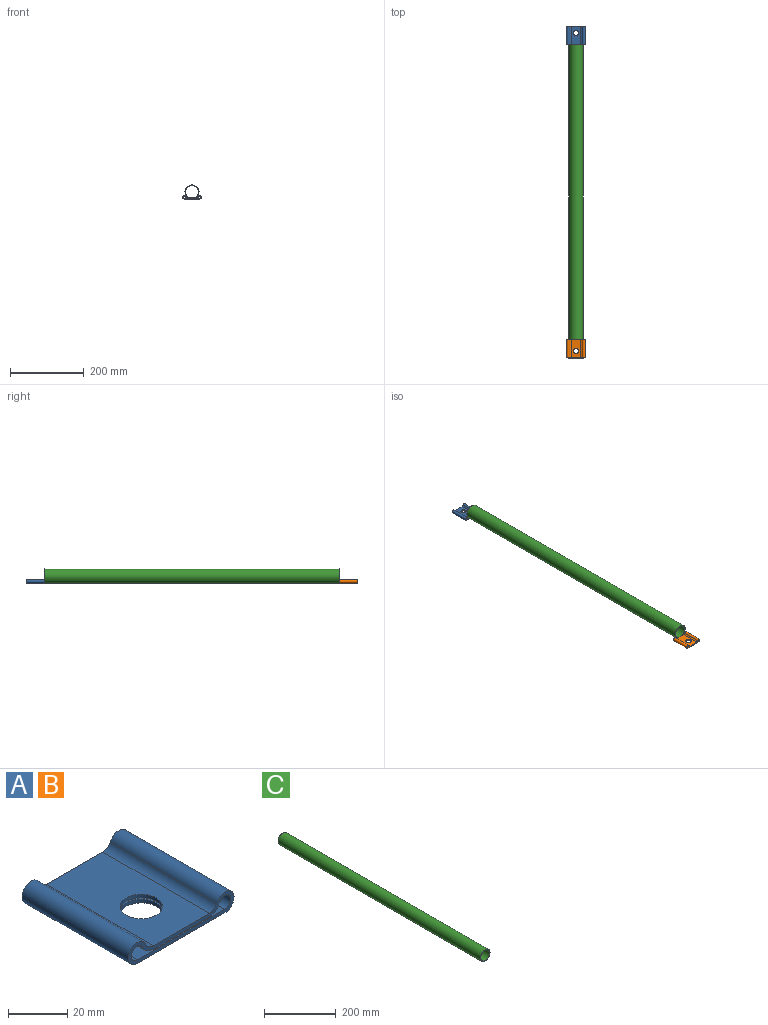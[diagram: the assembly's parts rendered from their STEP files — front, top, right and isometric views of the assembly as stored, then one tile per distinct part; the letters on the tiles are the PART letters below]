
ASSEMBLY  parts=3 mates=2
PART A: 16 faces, bbox 50.5x50.8x8.6 mm
  f0: cylinder r=3.81mm len=50.8mm, axis (0,1,0), area 230.1mm2, adj f1,f11,f12,f13
  f1: cylinder r=4.32mm len=50.8mm, axis (0,1,0), area 949.9mm2, adj f0,f2,f12,f13
  f2: plane 50.8x41.91mm, normal (0,0,-1), area 1968.7mm2, adj f1,f3,f12,f13,f15
  f3: cylinder r=4.32mm len=50.8mm, axis (0,1,0), area 949.9mm2, adj f2,f4,f12,f13
  f4: cylinder r=3.81mm len=50.8mm, axis (0,1,0), area 230.1mm2, adj f3,f11,f12,f13
  f5: plane 50.8x26.83mm, normal (0,0,-1), area 1202.4mm2, adj f6,f10,f12,f13,f14
  f6: cylinder r=5.28mm len=50.8mm, axis (0,1,0), area 319.1mm2, adj f5,f7,f12,f13
  f7: cylinder r=2.84mm len=50.8mm, axis (0,1,0), area 625.8mm2, adj f6,f8,f12,f13
  f8: plane 50.8x41.91mm, normal (0,0,1), area 1968.7mm2, adj f7,f9,f12,f13,f15
  f9: cylinder r=2.84mm len=50.8mm, axis (0,1,0), area 625.8mm2, adj f8,f10,f12,f13
  f10: cylinder r=5.28mm len=50.8mm, axis (0,1,0), area 319.1mm2, adj f5,f9,f12,f13
  f11: plane 50.8x26.83mm, normal (0,0,1), area 1202.4mm2, adj f0,f4,f12,f13,f14
  f12: plane 50.55x8.64mm, normal (0,-1,0), area 162.9mm2, adj f0,f1,f2,f3,f4,f5,f6,f7
  f13: plane 50.55x8.64mm, normal (0,1,0), area 162.9mm2, adj f0,f1,f2,f3,f4,f5,f6,f7
  f14: cylinder r=7.14mm len=14.29mm, axis (0,0,-1), area 66.1mm2, adj f5,f11
  f15: cylinder r=7.14mm len=14.29mm, axis (0,0,-1), area 66.1mm2, adj f2,f8
PART B: same geometry as A
PART C: 4 faces, bbox 38.1x800.1x38.1 mm
  f0: cylinder r=17.4mm len=800.1mm, axis (0,1,0), area 87467.8mm2, adj f2,f3
  f1: cylinder r=19.05mm len=800.1mm, axis (0,1,0), area 95767.7mm2, adj f2,f3
  f2: plane 38.1x38.1mm, normal (0,-1,0), area 189.1mm2, adj f0,f1
  f3: plane 38.1x38.1mm, normal (0,1,0), area 189.1mm2, adj f0,f1
PLACE A rot(axis=(0,0,1),180deg) t=(1.24,470.4,87.03)mm
PLACE B t=(1.24,-329.7,87.03)mm
PLACE C t=(1.24,70.35,87.03)mm
MATE fastened B.f13 <-> C.f2  axis (0,1,0) through (1.24,-329.7,87.03)mm
MATE fastened A.f13 <-> C.f3  axis (0,-1,0) through (1.24,470.4,87.03)mm
